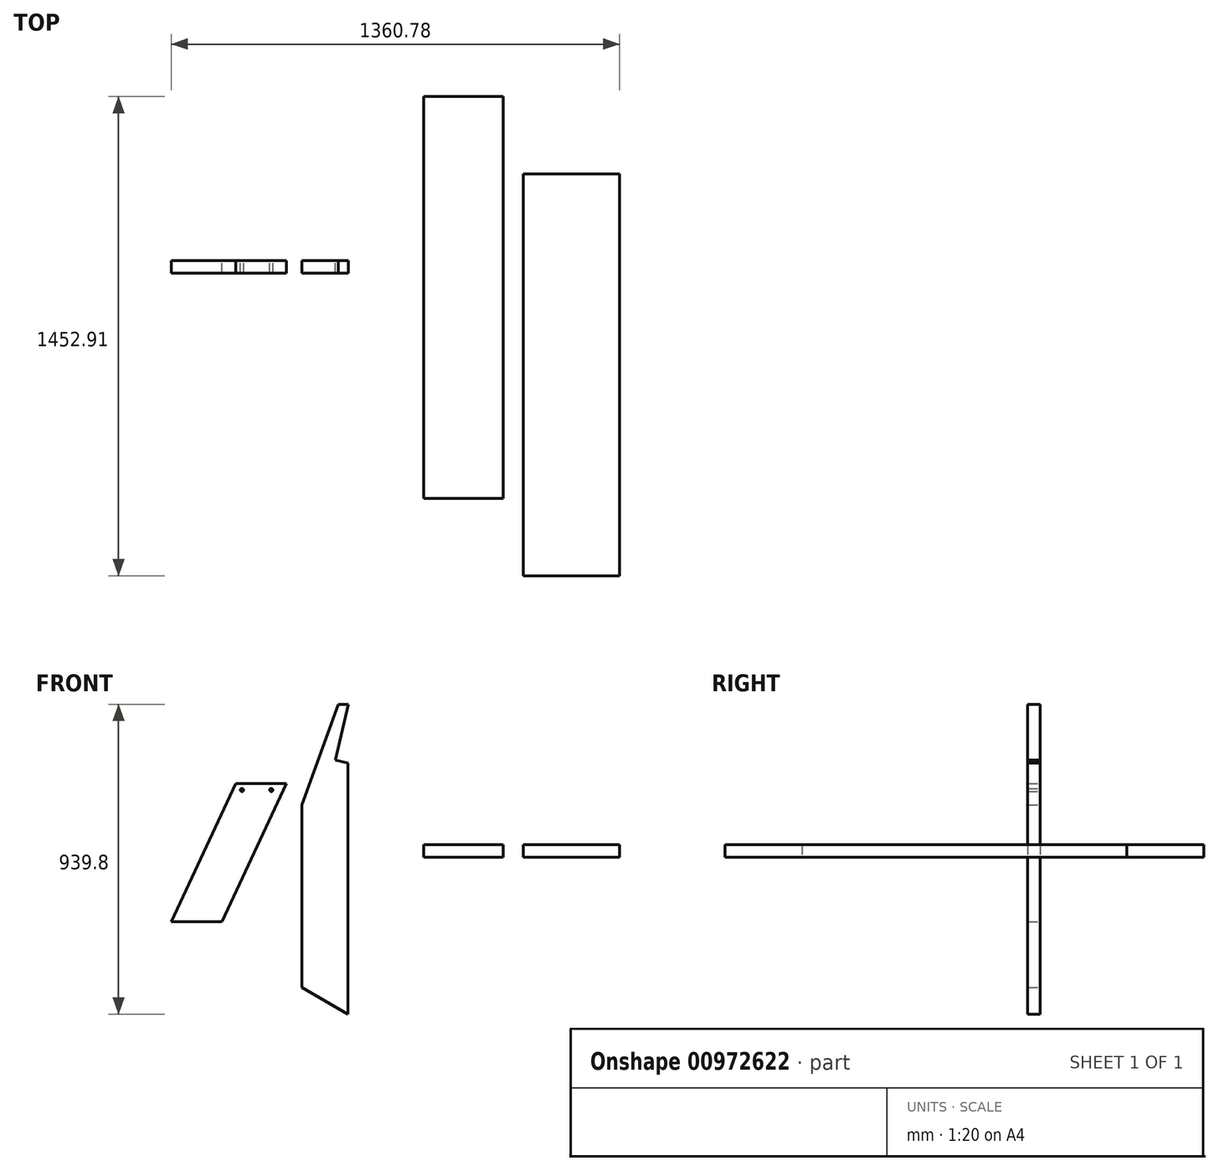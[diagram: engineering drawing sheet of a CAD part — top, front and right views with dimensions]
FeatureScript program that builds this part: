
annotation { "Feature Type Name" : "Feature", "Feature Type Description" : "" }
export const myFeature = defineFeature(function(context is Context, id is Id, definition is map)
    precondition{}
    {
        {
            var Q0;
            Q0=qCreatedBy(makeId("Front.planeOp"),FACE);
            var sketch = newSketch(context, id + "F0", { "sketchPlane" : qUnion([Q0])});
            skLineSegment(sketch, "E0.left", {"start": v(-234.05, 159.42) * mm, "end": v(-234.05, -394.93) * mm});
            skLineSegment(sketch, "E0.right", {"start": v(-94.35, 286.42) * mm, "end": v(-94.35, -475.58) * mm});
            skLineSegment(sketch, "E1", {"start": v(-123.11, 464.22) * mm, "end": v(-234.05, 159.42) * mm});
            skLineSegment(sketch, "E2", {"start": v(-94.35, -475.58) * mm, "end": v(-234.05, -394.93) * mm});
            skLineSegment(sketch, "E3", {"start": v(-131.47, 294.99) * mm, "end": v(-94.35, 286.42) * mm});
            skLineSegment(sketch, "E4", {"start": v(-131.47, 294.99) * mm, "end": v(-92.4, 464.22) * mm});
            skLineSegment(sketch, "E5", {"start": v(-92.4, 464.22) * mm, "end": v(-123.11, 464.22) * mm});
            skLineSegment(sketch, "E6", {"start": v(-234.05, 159.42) * mm, "end": v(-234.05, 528.9) * mm, "construction": true});
            skLineSegment(sketch, "E7", {"start": v(-94.35, -475.58) * mm, "end": v(-297.99, -475.58) * mm, "construction": true});
            skSolve(sketch);
        }
        {
            var Q0;
            Q0 = qSketchRegion(id + "F0", true);
            extrude(context, id + "F1", {"entities" : qUnion([Q0]), "depth" : 38.1 * mm, "offsetDistance" : 25.4 * mm});
        }
        {
            var Q0;
            Q0=qCreatedBy(makeId("Front.planeOp"),FACE);
            var sketch = newSketch(context, id + "F2", { "sketchPlane" : qUnion([Q0])});
            skLineSegment(sketch, "E8.bottom", {"start": v(-434.33, 223.18) * mm, "end": v(-280.19, 223.18) * mm});
            skLineSegment(sketch, "E8.top", {"start": v(-629.76, -195.92) * mm, "end": v(-475.62, -195.92) * mm});
            skLineSegment(sketch, "E8.left", {"start": v(-434.33, 223.18) * mm, "end": v(-629.76, -195.92) * mm});
            skLineSegment(sketch, "E8.right", {"start": v(-280.19, 223.18) * mm, "end": v(-475.62, -195.92) * mm});
            skCircle(sketch, "E9", {"center": v(-415.28, 204.13) * mm, "radius": 4.76 * mm});
            skCircle(sketch, "E10.1.0.0", {"center": v(-326.38, 204.13) * mm, "radius": 4.76 * mm});
            skLineSegment(sketch, "E10.direction1", {"start": v(-415.28, 204.13) * mm, "end": v(-326.38, 204.13) * mm, "construction": true});
            skSolve(sketch);
        }
        {
            var Q0;
            Q0 = qSketchRegion(id + "F2", true);
            extrude(context, id + "F3", {"entities" : qUnion([Q0]), "depth" : 38.1 * mm, "offsetDistance" : 25.4 * mm});
        }
        {
            var Q0;
            Q0=qCreatedBy(makeId("Top.planeOp"),FACE);
            var sketch = newSketch(context, id + "F4", { "sketchPlane" : qUnion([Q0])});
            skLineSegment(sketch, "E11.bottom", {"start": v(438.92, -956.01) * mm, "end": v(731.02, -956.01) * mm});
            skLineSegment(sketch, "E11.top", {"start": v(438.92, 263.19) * mm, "end": v(731.02, 263.19) * mm});
            skLineSegment(sketch, "E11.left", {"start": v(438.92, -956.01) * mm, "end": v(438.92, 263.19) * mm});
            skLineSegment(sketch, "E11.right", {"start": v(731.02, -956.01) * mm, "end": v(731.02, 263.19) * mm});
            skSolve(sketch);
        }
        {
            var Q0;
            Q0 = qSketchRegion(id + "F4", true);
            extrude(context, id + "F5", {"entities" : qUnion([Q0]), "depth" : 38.1 * mm, "offsetDistance" : 25.4 * mm});
        }
        {
            var Q0;
            Q0=qCreatedBy(makeId("Top.planeOp"),FACE);
            var sketch = newSketch(context, id + "F6", { "sketchPlane" : qUnion([Q0])});
            skLineSegment(sketch, "E12.bottom", {"start": v(136.22, 496.9) * mm, "end": v(377.52, 496.9) * mm});
            skLineSegment(sketch, "E12.top", {"start": v(136.22, -722.3) * mm, "end": v(377.52, -722.3) * mm});
            skLineSegment(sketch, "E12.left", {"start": v(136.22, 496.9) * mm, "end": v(136.22, -722.3) * mm});
            skLineSegment(sketch, "E12.right", {"start": v(377.52, 496.9) * mm, "end": v(377.52, -722.3) * mm});
            skSolve(sketch);
        }
        {
            var Q0;
            Q0 = qSketchRegion(id + "F6", true);
            extrude(context, id + "F7", {"entities" : qUnion([Q0]), "depth" : 38.1 * mm, "offsetDistance" : 25.4 * mm});
        }
    });
